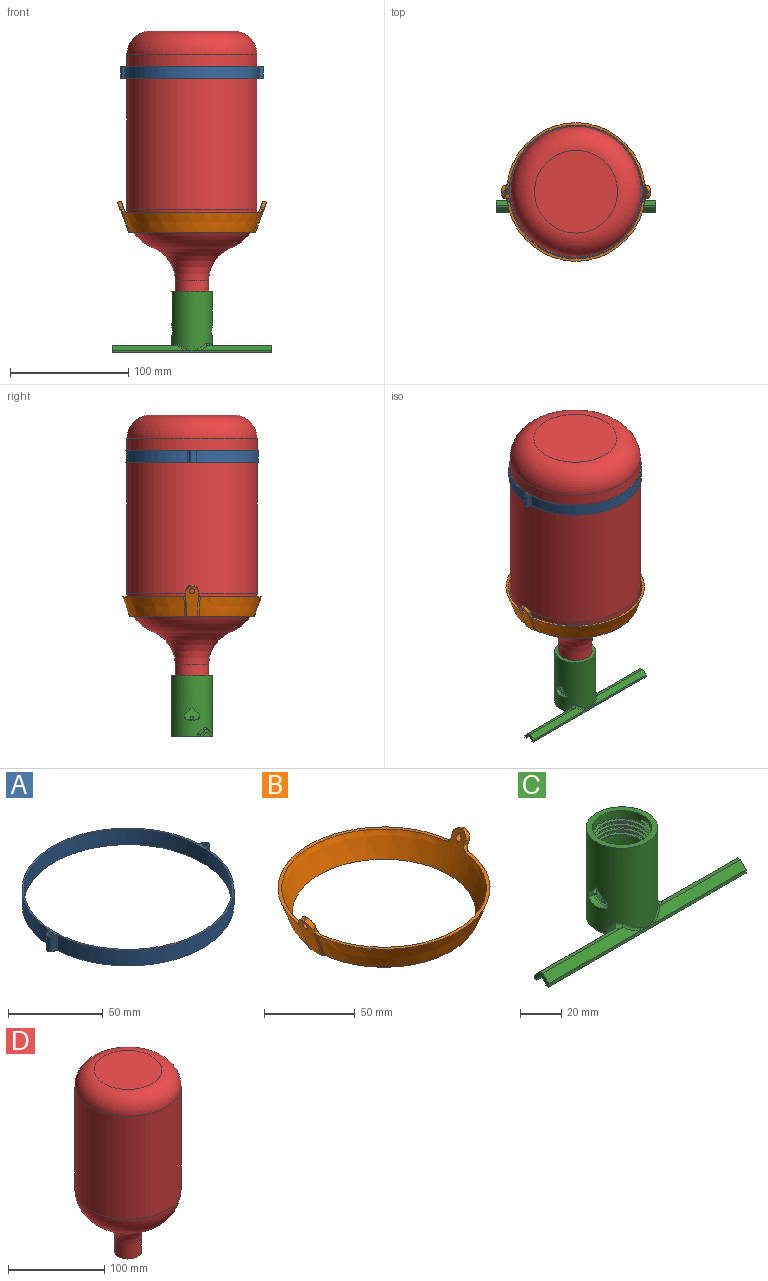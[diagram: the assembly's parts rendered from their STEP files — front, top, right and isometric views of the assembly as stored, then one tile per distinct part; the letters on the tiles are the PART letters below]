
ASSEMBLY  parts=4 mates=3
PART A: 13 faces, bbox 120x112x10 mm
  f0: cylinder r=56mm len=111.8mm, axis (0,0,-1), area 1691.5mm2, adj f3,f4,f5,f9
  f1: cylinder r=56mm len=111.8mm, axis (0,0,-1), area 1691.5mm2, adj f3,f4,f6,f11
  f2: cylinder r=55mm len=110mm, axis (0,0,-1), area 3455.8mm2, adj f3,f4
  f3: plane 120x112mm, normal (0,0,-1), area 369.9mm2, adj f0,f1,f2,f5,f6,f7,f8,f9
  f4: plane 120x112mm, normal (0,0,1), area 369.9mm2, adj f0,f1,f2,f5,f6,f7,f8,f9
  f5: cylinder r=1mm len=10mm, axis (0,0,-1), area 16.8mm2, adj f0,f3,f4,f7
  f6: cylinder r=1mm len=10mm, axis (0,0,-1), area 16.8mm2, adj f1,f3,f4,f7
  f7: cylinder r=2.5mm len=10mm, axis (0,0,-1), area 87.2mm2, adj f3,f4,f5,f6
  f8: cylinder r=1.5mm len=10mm, axis (0,0,-1), area 94.2mm2, adj f3,f4
  f9: cylinder r=1mm len=10mm, axis (0,0,-1), area 16.8mm2, adj f0,f3,f4,f10
  f10: cylinder r=2.5mm len=10mm, axis (0,0,-1), area 87.2mm2, adj f3,f4,f9,f11
  f11: cylinder r=1mm len=10mm, axis (0,0,-1), area 16.8mm2, adj f1,f3,f4,f10
  f12: cylinder r=1.5mm len=10mm, axis (0,0,-1), area 94.2mm2, adj f3,f4
PART B: 32 faces, bbox 184.1x120.5x37.4 mm
  f0: cone r=52.57mm half-angle=20deg, axis (0,0,1), area 2795.4mm2, adj f1,f5,f14,f16,f26,f28
  f1: plane 115.88x50.59mm, normal (0,0,1), area 329.2mm2, adj f0,f4,f14,f26
  f2: cone r=52.57mm half-angle=20deg, axis (0,0,1), area 2795.4mm2, adj f3,f5,f13,f15,f27,f29
  f3: plane 115.88x50.59mm, normal (0,0,1), area 329.2mm2, adj f2,f4,f13,f27
  f4: cone r=50.57mm half-angle=20deg, axis (0,0,1), area 6004.4mm2, adj f1,f3,f5,f7,f8,f9,f10,f11
  f5: plane 107.71x105.32mm, normal (0,0,-1), area 672.6mm2, adj f0,f2,f4,f6,f15,f16,f19,f28
  f6: cone r=53.76mm half-angle=20deg, axis (0,0,1), area 248.6mm2, adj f5,f7,f8,f9,f10,f11,f12,f15
  f7: cone r=60.15mm half-angle=70deg, axis (0,0,-1), area 1.3mm2, adj f4,f6,f17,f18
  f8: plane 3.63x2.26mm, normal (-0.09,1,0), area 5.6mm2, adj f4,f6,f13,f18
  f9: plane 3.63x2.26mm, normal (-0.09,-1,0), area 5.6mm2, adj f4,f6,f14,f17
  f10: plane 3.73x1.42mm, normal (0,0.71,-0.71), area 6.4mm2, adj f4,f6,f11,f12
  f11: cylinder r=2mm len=4.42mm, axis (-1,0,0), area 35.9mm2, adj f4,f6,f10,f12
  f12: plane 3.73x1.42mm, normal (0,-0.71,-0.71), area 6.4mm2, adj f4,f6,f10,f11
  f13: cylinder r=3mm len=4.61mm, axis (1,0.09,0), area 11.1mm2, adj f2,f3,f4,f8,f15
  f14: cylinder r=3mm len=4.61mm, axis (-1,0.09,0), area 11.1mm2, adj f0,f1,f4,f9,f16
  f15: bspline ~29.21x11.68mm, area 42mm2, adj f2,f5,f6,f13
  f16: bspline ~29.21x11.68mm, area 42mm2, adj f0,f5,f6,f14
  f17: bspline ~47.49x21.4mm, area 24mm2, adj f4,f6,f7,f9
  f18: bspline ~42.63x19.62mm, area 24mm2, adj f4,f6,f7,f8
  f19: cone r=53.76mm half-angle=20deg, axis (0,0,1), area 248.6mm2, adj f5,f20,f21,f22,f23,f24,f25,f28
  f20: cone r=60.15mm half-angle=70deg, axis (0,0,-1), area 1.3mm2, adj f4,f19,f30,f31
  f21: plane 3.63x2.26mm, normal (0.09,-1,0), area 5.6mm2, adj f4,f19,f26,f31
  f22: plane 3.63x2.26mm, normal (0.09,1,0), area 5.6mm2, adj f4,f19,f27,f30
  f23: plane 3.73x1.42mm, normal (0,-0.71,-0.71), area 6.4mm2, adj f4,f19,f24,f25
  f24: cylinder r=2mm len=4mm, axis (1,0,0), area 30.1mm2, adj f4,f19,f23,f25
  f25: plane 3.73x1.42mm, normal (0,0.71,-0.71), area 6.4mm2, adj f4,f19,f23,f24
  f26: cylinder r=3mm len=4.61mm, axis (-1,-0.09,0), area 11.1mm2, adj f0,f1,f4,f21,f28
  f27: cylinder r=3mm len=4.61mm, axis (1,-0.09,0), area 11.1mm2, adj f2,f3,f4,f22,f29
  f28: bspline ~29.21x11.68mm, area 42mm2, adj f0,f5,f19,f26
  f29: bspline ~29.21x11.68mm, area 42mm2, adj f2,f5,f19,f27
  f30: bspline ~47.49x21.4mm, area 24mm2, adj f4,f19,f20,f22
  f31: bspline ~42.63x19.62mm, area 24mm2, adj f4,f19,f20,f21
PART C: 80 faces, bbox 140.6x40.6x58 mm
  f0: bspline ~1.31x1.14mm, area 0.4mm2, adj f23,f55,f57
  f1: bspline ~1.92x1.76mm, area 1.2mm2, adj f21,f30,f60,f63
  f2: bspline ~1.31x1.14mm, area 0.4mm2, adj f24,f61,f64
  f3: bspline ~1.6x1.44mm, area 1.2mm2, adj f26,f33,f66,f67
  f4: cylinder r=17.3mm len=52mm, axis (0,0,1), area 5218mm2, adj f13,f19,f20,f21,f22,f23,f24,f25
  f5: cylinder r=17.3mm len=6.51mm, axis (0,0,1), area 23.6mm2, adj f13,f48,f49,f50,f51,f52
  f6: cylinder r=14.3mm len=28.6mm, axis (0,0,1), area 301mm2, adj f10,f14,f16,f29
  f7: cylinder r=14.3mm len=28.6mm, axis (0,0,1), area 1469.5mm2, adj f8,f15,f18,f19,f20,f21,f23,f24
  f8: cylinder r=14.3mm len=28.6mm, axis (0,0,1), area 43.3mm2, adj f7,f9,f16,f18
  f9: cylinder r=14.3mm len=28.6mm, axis (0,0,1), area 43.3mm2, adj f8,f10,f16,f18
  f10: cylinder r=14.3mm len=28.6mm, axis (0,0,1), area 43.3mm2, adj f6,f9,f16,f18
  f11: cylinder r=14.3mm len=28.6mm, axis (0,0,1), area 1468.6mm2, adj f13,f31,f32
  f12: cylinder r=17.3mm len=6.51mm, axis (0,0,1), area 23.6mm2, adj f13,f37,f38,f39,f40,f41
  f13: plane 134.6x34.6mm, normal (0,0,-1), area 757.4mm2, adj f4,f5,f11,f12,f36,f37,f41,f42
  f14: plane 2.23x1.61mm, normal (0,1,0), area 1.5mm2, adj f6,f16,f17,f18
  f15: plane 2.23x1.61mm, normal (0,-1,0), area 1.5mm2, adj f7,f16,f17,f18
  f16: bspline ~33.02x28.6mm, area 199.3mm2, adj f6,f8,f9,f10,f14,f15,f17
  f17: bspline ~32.26x27.94mm, area 432.6mm2, adj f14,f15,f16,f18
  f18: bspline ~33.02x28.6mm, area 767.9mm2, adj f7,f8,f9,f10,f14,f15,f17
  f19: plane 6.62x6.62mm, normal (0,0.71,-0.71), area 28.1mm2, adj f4,f7,f20,f23
  f20: plane 6.62x6.62mm, normal (0,-0.71,-0.71), area 28.1mm2, adj f4,f7,f19,f21
  f21: plane 3.49x3.21mm, normal (0,-1,0), area 9.9mm2, adj f1,f4,f7,f20,f22,f60
  f22: cylinder r=14mm len=12.87mm, axis (1,0,0), area 44mm2, adj f4,f21,f23,f57
  f23: plane 3.49x3.21mm, normal (0,1,0), area 9.9mm2, adj f0,f4,f7,f19,f22,f55
  f24: plane 3.49x3.21mm, normal (0,1,0), area 9.9mm2, adj f2,f4,f7,f25,f28,f61
  f25: cylinder r=14mm len=12.87mm, axis (1,0,0), area 52.3mm2, adj f4,f24,f26,f64
  f26: plane 3.49x3.21mm, normal (0,-1,0), area 9.9mm2, adj f3,f4,f7,f25,f27,f66
  f27: plane 6.62x6.62mm, normal (0,-0.71,-0.71), area 28.1mm2, adj f4,f7,f26,f28
  f28: plane 6.62x6.62mm, normal (0,0.71,-0.71), area 28.1mm2, adj f4,f7,f24,f27
  f29: plane 34.6x34.6mm, normal (0,0,1), area 297.8mm2, adj f4,f6
  f30: plane 26.46x12.43mm, normal (-0.71,0,0.71), area 338mm2, adj f1,f55,f56,f57,f62,f63,f79
  f31: plane 28.6x14.3mm, normal (0.71,0,-0.71), area 444.3mm2, adj f11,f32,f79
  f32: plane 34.61x20.31mm, normal (-0.71,0,-0.71), area 444.3mm2, adj f11,f31,f78
  f33: plane 26.46x12.43mm, normal (0.71,0,0.71), area 338mm2, adj f3,f58,f61,f62,f64,f67,f78
  f34: plane 53.32x2.22mm, normal (0,0,1), area 105mm2, adj f35,f43,f44,f76,f77
  f35: plane 62.77x4.47mm, normal (0,-0.71,0.71), area 328.1mm2, adj f34,f36,f44,f75,f77
  f36: plane 135.1x2.5mm, normal (0,-1,0), area 269.2mm2, adj f13,f35,f44,f53,f54,f72,f73
  f37: plane 59.23x1.17mm, normal (0,1,0), area 69.4mm2, adj f12,f13,f38,f44
  f38: plane 59.46x2.82mm, normal (0,0.71,-0.71), area 209.1mm2, adj f12,f37,f39,f44
  f39: plane 55.57x0.83mm, normal (0,0,-1), area 45.9mm2, adj f12,f38,f40,f44
  f40: plane 54.82x2.68mm, normal (0,-0.71,-0.71), area 196.1mm2, adj f12,f39,f41,f44
  f41: plane 52.71x1.17mm, normal (0,-1,0), area 61.8mm2, adj f12,f13,f40,f44
  f42: plane 48.74x2mm, normal (0,1,0), area 97.5mm2, adj f13,f43,f44,f74
  f43: plane 50.73x4.01mm, normal (0,0.71,0.71), area 281.3mm2, adj f34,f42,f44,f74,f76
  f44: plane 10x6mm, normal (1,0,0), area 28.1mm2, adj f13,f34,f35,f36,f37,f38,f39,f40
  f45: plane 53.32x2.22mm, normal (0,0,1), area 105mm2, adj f46,f53,f54,f69,f70
  f46: plane 50.73x4.01mm, normal (0,0.71,0.71), area 281.3mm2, adj f45,f47,f54,f68,f69
  f47: plane 48.74x2mm, normal (0,1,0), area 97.5mm2, adj f13,f46,f54,f68
  f48: plane 52.71x1.17mm, normal (0,-1,0), area 61.8mm2, adj f5,f13,f49,f54
  f49: plane 54.82x2.68mm, normal (0,-0.71,-0.71), area 196.1mm2, adj f5,f48,f50,f54
  f50: plane 55.57x0.83mm, normal (0,0,-1), area 45.9mm2, adj f5,f49,f51,f54
  f51: plane 59.46x2.82mm, normal (0,0.71,-0.71), area 209.1mm2, adj f5,f50,f52,f54
  f52: plane 59.23x1.17mm, normal (0,1,0), area 69.4mm2, adj f5,f13,f51,f54
  f53: plane 62.77x4.47mm, normal (0,-0.71,0.71), area 328.1mm2, adj f36,f45,f54,f70,f71
  f54: plane 10x6mm, normal (-1,0,0), area 28.1mm2, adj f13,f36,f45,f46,f47,f48,f49,f50
  f55: bspline ~1.6x1.44mm, area 1.2mm2, adj f0,f23,f30,f56
  f56: bspline ~15.18x14.76mm, area 34.5mm2, adj f7,f30,f55,f59
  f57: bspline ~14.23x3.06mm, area 16.4mm2, adj f0,f22,f30,f60
  f58: bspline ~15.18x14.76mm, area 34.5mm2, adj f7,f33,f59,f61
  f59: bspline ~3.58x1.54mm, area 3.6mm2, adj f7,f56,f58,f62
  f60: bspline ~1.38x1.18mm, area 0.4mm2, adj f1,f21,f57
  f61: bspline ~1.92x1.76mm, area 1.2mm2, adj f2,f24,f33,f58
  f62: cylinder r=1mm len=26.45mm, axis (0,1,0), area 41.5mm2, adj f30,f33,f59,f65
  f63: bspline ~15.18x14.76mm, area 34.5mm2, adj f1,f7,f30,f65
  f64: bspline ~14.12x2.96mm, area 16.4mm2, adj f2,f25,f33,f66
  f65: bspline ~3.58x1.54mm, area 3.6mm2, adj f7,f62,f63,f67
  f66: bspline ~1.38x1.18mm, area 0.4mm2, adj f3,f26,f64
  f67: bspline ~15.18x14.76mm, area 34.5mm2, adj f3,f7,f33,f65
  f68: cylinder r=2mm len=2.83mm, axis (0,0,1), area 8.3mm2, adj f4,f13,f46,f47,f69
  f69: bspline ~7.14x6.6mm, area 23.4mm2, adj f4,f45,f46,f68,f70
  f70: torus R=19.3mm, axis (0,0,1), area 11.1mm2, adj f4,f45,f53,f69,f71
  f71: bspline ~8.92x6mm, area 18.2mm2, adj f4,f53,f70,f72
  f72: bspline ~5.91x1.69mm, area 2.4mm2, adj f4,f36,f71
  f73: bspline ~5.91x1.69mm, area 2.4mm2, adj f4,f36,f75
  f74: cylinder r=2mm len=2.83mm, axis (0,0,1), area 8.3mm2, adj f4,f13,f42,f43,f76
  f75: bspline ~8.92x6mm, area 18.2mm2, adj f4,f35,f73,f77
  f76: bspline ~7.14x6.6mm, area 23.4mm2, adj f4,f34,f43,f74,f77
  f77: torus R=19.3mm, axis (0,0,-1), area 11.1mm2, adj f4,f34,f35,f75,f76
  f78: cylinder r=1.5mm len=5.85mm, axis (0,0,-1), area 26.7mm2, adj f32,f33
  f79: cylinder r=1.5mm len=5.85mm, axis (0,0,-1), area 26.7mm2, adj f30,f31
PART D: 13 faces, bbox 119.1x119.1x230 mm
  f0: plane 28x28mm, normal (0,0,-1), area 84.8mm2, adj f1,f7
  f1: cylinder r=14mm len=28mm, axis (0,0,-1), area 1660.6mm2, adj f0,f2
  f2: torus R=44mm, axis (0,0,-1), area 4636mm2, adj f1,f3
  f3: torus R=20mm, axis (0,0,-1), area 12398.4mm2, adj f2,f4
  f4: cylinder r=55mm len=130.71mm, axis (0,0,-1), area 45171.8mm2, adj f3,f5
  f5: torus R=35mm, axis (0,0,-1), area 9422mm2, adj f4,f6
  f6: plane 70x70mm, normal (0,0,1), area 3848.5mm2, adj f5
  f7: cylinder r=13mm len=26mm, axis (0,0,-1), area 1542mm2, adj f0,f8
  f8: torus R=44mm, axis (0,0,-1), area 4609.6mm2, adj f7,f9
  f9: torus R=20mm, axis (0,0,-1), area 11845.6mm2, adj f8,f10
  f10: cylinder r=54mm len=130.71mm, axis (0,0,-1), area 44350.5mm2, adj f9,f11
  f11: torus R=35mm, axis (0,0,-1), area 8831.5mm2, adj f10,f12
  f12: plane 70x70mm, normal (0,0,-1), area 3848.5mm2, adj f11
PLACE A t=(-14.71,27.98,171.72)mm
PLACE B t=(-14.71,27.98,41.7)mm
PLACE C t=(-14.71,27.98,-60.28)mm
PLACE D t=(-14.71,27.98,-18.28)mm
MATE slider B.f0 <-> D.f1  axis (0,0,1) through (-14.71,27.98,54.85)mm
MATE fastened D.f1 <-> C.f4  axis (0,0,-1) through (-14.71,27.98,-18.28)mm
MATE fastened A.f0 <-> D.f1  axis (0,0,-1) through (-14.71,27.98,171.72)mm
